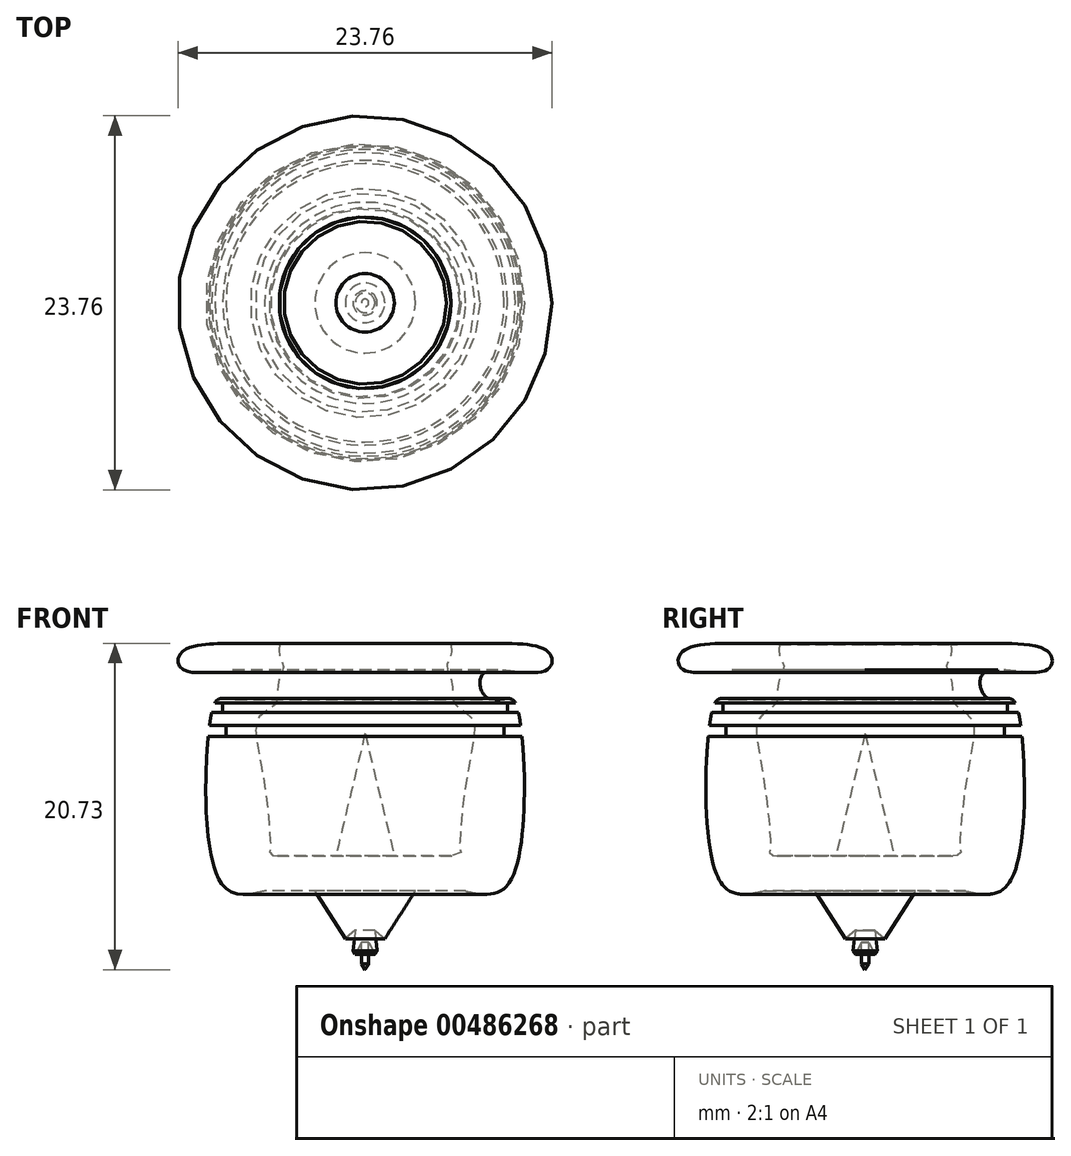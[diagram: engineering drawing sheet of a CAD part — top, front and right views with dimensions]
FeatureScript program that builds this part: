
annotation { "Feature Type Name" : "Feature", "Feature Type Description" : "" }
export const myFeature = defineFeature(function(context is Context, id is Id, definition is map)
    precondition{}
    {
        {
            var Q0;
            Q0=qCreatedBy(makeId("Front.planeOp"),FACE);
            var sketch = newSketch(context, id + "F0", { "sketchPlane" : qUnion([Q0])});
            skLineSegment(sketch, "E0", {"start": v(0, 20) * mm, "end": v(0, 0) * mm, "construction": true});
            skLineSegment(sketch, "E1", {"start": v(5.45, 2.22) * mm, "end": v(1.86, 2.22) * mm});
            skLineSegment(sketch, "E2", {"start": v(0, 2.22) * mm, "end": v(0, 0) * mm});
            skFitSpline(sketch, "E3", {"points": [v(3.2, 0) * mm, v(6.38, 0) * mm], "startDerivative": vector(2.86, 0) * mm, "endDerivative": vector(2.86, 0) * mm});
            skFitSpline(sketch, "E4", {"points": [v(6.38, 0) * mm, v(9.16, 0.53) * mm, v(9.74, 11.35) * mm, v(9.09, 12.23) * mm, v(7.71, 12.3) * mm, v(7.54, 13.83) * mm, v(11.45, 14) * mm, v(11.73, 15.09) * mm, v(5.45, 15.66) * mm], "startDerivative": vector(26.06, -5.9) * mm, "endDerivative": vector(-51.19, -1.14) * mm});
            skFitSpline(sketch, "E5", {"points": [v(5.45, 15.66) * mm, v(5.45, 14.93) * mm, v(5.16, 14.28) * mm, v(5.45, 13.5) * mm, v(5.57, 12.26) * mm, v(5.75, 11.8) * mm, v(6.77, 11) * mm, v(6.88, 9.64) * mm, v(6.2, 5.33) * mm, v(6.01, 3.1) * mm, v(6.01, 2.75) * mm, v(5.45, 2.22) * mm], "startDerivative": vector(-0.13, -14.36) * mm, "endDerivative": vector(-33.68, 1.42) * mm});
            skLineSegment(sketch, "E6", {"start": v(9.54, 11.96) * mm, "end": v(9.04, 11.96) * mm});
            skLineSegment(sketch, "E7", {"start": v(9.04, 11.96) * mm, "end": v(9.04, 11.35) * mm});
            skLineSegment(sketch, "E8", {"start": v(9.04, 11.35) * mm, "end": v(9.74, 11.35) * mm});
            skLineSegment(sketch, "E9", {"start": v(9.88, 10.5) * mm, "end": v(8.84, 10.5) * mm});
            skLineSegment(sketch, "E10", {"start": v(8.84, 10.5) * mm, "end": v(8.84, 9.82) * mm});
            skLineSegment(sketch, "E11", {"start": v(8.84, 9.82) * mm, "end": v(9.96, 9.82) * mm});
            skLineSegment(sketch, "E12", {"start": v(9.96, 9.82) * mm, "end": v(10.43, 9.24) * mm});
            skLineSegment(sketch, "E13", {"start": v(10.43, 9.24) * mm, "end": v(10.01, 9.24) * mm});
            skLineSegment(sketch, "E14", {"start": v(10.04, 8.87) * mm, "end": v(10.48, 8.55) * mm});
            skLineSegment(sketch, "E15", {"start": v(10.48, 8.55) * mm, "end": v(10.06, 8.55) * mm});
            skLineSegment(sketch, "E16", {"start": v(10.08, 8.13) * mm, "end": v(10.74, 7.8) * mm});
            skLineSegment(sketch, "E17", {"start": v(10.74, 7.8) * mm, "end": v(10.1, 7.8) * mm});
            skLineSegment(sketch, "E18", {"start": v(1.86, 2.22) * mm, "end": v(0, 10) * mm});
            skLineSegment(sketch, "E19", {"start": v(0, 10) * mm, "end": v(0, 2.22) * mm});
            skLineSegment(sketch, "E20", {"start": v(3.2, 0) * mm, "end": v(1.25, -3.04) * mm});
            skLineSegment(sketch, "E21", {"start": v(0, -5) * mm, "end": v(0, 0) * mm});
            skLineSegment(sketch, "E22", {"start": v(-2.47, 0) * mm, "end": v(-2.47, 10.13) * mm});
            skLineSegment(sketch, "E23", {"start": v(0.23, -4.64) * mm, "end": v(0.23, -3.25) * mm});
            skLineSegment(sketch, "E24", {"start": v(0.23, -3.25) * mm, "end": v(0.62, -4.03) * mm});
            skLineSegment(sketch, "E25", {"start": v(0.77, -3.8) * mm, "end": v(0.62, -2.5) * mm});
            skPoint(sketch, "E25.endSnap0", {"position": v(0, -2.5) * mm});
            skLineSegment(sketch, "E26", {"start": v(0.62, -2.5) * mm, "end": v(1.25, -3.04) * mm});
            skLineSegment(sketch, "E27.trimOffspring", {"start": v(0.77, -3.8) * mm, "end": v(0.62, -4.03) * mm});
            skLineSegment(sketch, "E28.trimOffspring", {"start": v(0.23, -4.64) * mm, "end": v(0, -5) * mm});
            skSolve(sketch);
        }
        {
            var Q0;
            Q0=makeQuery(id+"F0.imprint","IMPRINT",FACE,{"disambiguationData":[TD([[makeQuery(id+"F0.imprint","IMPRINT",EDGE,{"derivedFrom":sQuery(id+"F0.wireOp",EDGE,"uJ4eU5tt-ll4T-G1n1-Olee-nEpkercioOpn")}),1.0]])]});
            var Q1;
            Q1=makeQuery(id+"F0.imprint","IMPRINT",FACE,{"disambiguationData":[TD([[makeQuery(id+"F0.imprint","IMPRINT",EDGE,{"derivedFrom":sQuery(id+"F0.wireOp",EDGE,"E1")}),1.0]])]});
            var Q2;
            Q2=sQuery(id+"F0.wireOp",EDGE,"E0");
            revolve(context, id + "F1", {"entities" : qUnion([Q0, Q1]), "axis" : qUnion([Q2]), "revolveType" : RevolveType.FULL});
        }
    });
